# Revit family: Multiline Channel_ with grating - 24-05-2016 9
name_source: partatom
category: Generic Models
revit_build: Autodesk Revit 2014 (Build: 20130308_1515(x64)
units: mm (PartAtom-declared; Revit-internal decimal feet)

## types (12) — shared parameters
Anschrift = Postfach 320, 24755 Rendsburg
Assembly Code = D2040
Belastungsklasse = A 15 - E 600
Beschreibung = Entwässerungsrinne
Bottom depth = 20 mm  [stored 0.0656168 ft]
Breite = 135 mm  [stored 0.442913 ft]
Cut dist = 15.08 mm
Deponierfähigkeit Material Rinnenkörper = Abfallschlüssel 170107 gem. Verordnung über das Europäische Abfallverzeichnis
Einbauempfehlung, Qualität und Menge Ummantelungsbeton = http://www.aco-tiefbau.de
Einbauempfehlungen = http://www.aco-tiefbau.de
Farbe Kantenschutz = silber
Farbe Rinnenkörper = braun
Fax = +40 (0) 4331 354358
Front void end(Common) = -12 mm  [stored -0.0393701 ft]
Gasket = Yes
Gasket end = 9.13 mm  [stored 0.0299541 ft]
L projection end = -82.5 mm
L projection start = -67.5 mm  [stored -0.221457 ft]
Lieferant = ACO Tiefbau Vertrieb GmbH
Material Kantenschutz = Stahl
Material Rinnenkörper = ACO Polymerbeton
Norm = DIN EN 1433:2002, CE - Kennzeichnung
Oberflächenschutz Kantenschutz = verzinkt
Preis / Stck = http://www.aco-tiefbau.de
Produktbroschüre = http://www.aco-tiefbau.de
Produktinformationen = http://www.aco-tiefbau.de
Produktname = ACO DRAIN Multiline V 100 S
R projection start = 67.5 mm  [stored 0.221457 ft]
Recyclingfähigkeit Material Kantenschutz = voll recyclingfähig
Recyclingfähigkeit Material Rinnenkörper = voll recyclingfähig
Telefon = +49 (0) 4331 354 500
URL = www.aco-tiefbau.de
Version = 1
entwickelt von = www.aco-tiefbau.de
hydraulische Leistungsfähigkeit = e_mail anwendungstechnik

## per-type parameters (varying)
| type | Abmessungen | Artikelnummer | Betreibs- und Wartungshinweise | Channel article number | Channel price / stk | Channel weight ( Kg ) | Channnel dimensions( L x W x H) | Gewicht | Grating | Grating number | Höhe | Länge | Outlet end | Outlet start | Profile | Projection | R projection end | Rear extrusion end | Rear extrusion start | Side cut | Type Comments | Void depth |
| 132330- Channel_1000_ lg_150_ht | 1000mm x 135mm x 150mm (LxWxH | 132330 | http://www.aco-tiefbau.de | 132330 | 57.25 EUR | 16.8 | 1000 x 135 x 150 | 15,0 Kg | A15 : 12665-Lochrost Edelstahl_500mm lang_1.4 kg | 1 | 150 mm | 1000 mm | -702 mm  [stored -2.30315 ft] | -700 mm  [stored -2.29659 ft] | 79 mm | No | 82.5 mm | -1011 mm  [stored -3.31693 ft] | -1000 mm  [stored -3.28084 ft] | 56.5 mm  [stored 0.185367 ft] | "ACO DRAIN Multiline V100S 0.0, Rinnenkörper ohne Sohlengefälle, 
serienmäßig mit EPDM Dichtung, 1000mm lang" | 93.5 mm |
| 132340- Channel_1000_ lg_175_ht | 1000mm x 135mm x 175mm (LxWxH) | 132340 | http://www.aco-tiefbau.de | 132340 | 57.25 EUR | 18.9 | 1000 x 135 x 175 | 17,1 Kg |  | 1 | 175 mm | 1000 mm | -702 mm  [stored -2.30315 ft] | -700 mm  [stored -2.29659 ft] | 104 mm  [stored 0.341207 ft] | No | 82.5 mm | -1011 mm  [stored -3.31693 ft] | -1000 mm  [stored -3.28084 ft] | 81.5 mm  [stored 0.267388 ft] | "ACO DRAIN Multiline V100S 5.0, Rinnenkörper ohne Sohlengefälle, 
serienmäßig mit EPDM Dichtung, 1000mm lang" | 118.5 mm  [stored 0.38878 ft] |
| 132350- Channel_1000_ lg_200_ht | 1000mm x 135mm x 200mm (LxWxH) | 132350 | http://www.aco-tiefbau.de | 132350 | 57.25 EUR | 21.0 | 1000 x 135 x 200 | 19,6 Kg |  | 2 | 200 mm | 1000 mm | -702 mm  [stored -2.30315 ft] | -700 mm  [stored -2.29659 ft] | 129 mm  [stored 0.423228 ft] | No | 82.5 mm | -1011 mm  [stored -3.31693 ft] | -1000 mm  [stored -3.28084 ft] | 106.5 mm  [stored 0.349409 ft] | "ACO DRAIN Multiline V100S 10.0, Rinnenkörper ohne Sohlengefälle, 
serienmäßig mit EPDM Dichtung, 1000mm lang" | 143.5 mm  [stored 0.470801 ft] |
| 132370- Channel_1000_ lg_250_ht | 1000mm x 135mm x 250mm (LxWxH) | 132370 | http://www.aco-tiefbau.de | 132370 | 57.25 EUR | 24.9 | 1000 x 135 x 250 | 22,3 Kg |  | 1 | 250 mm | 1000 mm | -702 mm  [stored -2.30315 ft] | -700 mm  [stored -2.29659 ft] | 179 mm | No | 82.5 mm | -1011 mm  [stored -3.31693 ft] | -1000 mm  [stored -3.28084 ft] | 156.5 mm | "ACO DRAIN Multiline V100S 20.0, Rinnenkörper ohne Sohlengefälle, 
serienmäßig mit EPDM Dichtung, 1000mm lang" | 193.5 mm |
| 132332- Channel_500_ lg_150_ht | 500mm x 135mm x 150mm (LxWxH) | 132332 | http://www.aco-tiefbau.de | 132332 | 43.50 EUR | 9.5 | 500 x 135 x 150 | 8,5 Kg |  | 2 | 150 mm | 500 mm | -135 mm | -51 mm | 79 mm | No | 82.5 mm | -511 mm  [stored -1.67651 ft] | -500 mm  [stored -1.64042 ft] | 56.5 mm  [stored 0.185367 ft] | "ACO DRAIN Multiline V100S 0.1, Rinnenkörper ohne Sohlengefälle, 
serienmäßig mit EPDM Dichtung, 500mm lang, mit seitlichen Vorformungen für Eck-, T- und Kreuzverbindungen" | 93.5 mm |
| 132342- Channel_500_ lg_175_ht | 500mm x 135mm x 175mm (LxWxH) | 132342 | http://www.aco-tiefbau.de | 132342 | 43.50 EUR | 10.6 | 500 x 135 x 175 | 9,4 Kg |  | 2 | 175 mm | 500 mm | -160 mm  [stored -0.524934 ft] | -51 mm | 104 mm  [stored 0.341207 ft] | No | 82.5 mm | -511 mm  [stored -1.67651 ft] | -500 mm  [stored -1.64042 ft] | 81.5 mm  [stored 0.267388 ft] | "ACO DRAIN Multiline V100S 5.1, Rinnenkörper ohne Sohlengefälle, serienmäßig mit EPDM Dichtung, 500mm lang, 
mit seitlichen Vorformungen für Eck-, T- und Kreuzverbindungen" | 118.5 mm  [stored 0.38878 ft] |
| 132352- Channel_500_ lg_200_ht | 500mm x 135mm x 200mm (LxWxH) | 132352 | http://www.aco-tiefbau.de
http://www.aco-tiefbau.de | 132352 | 43.50 EUR | 11.7 | 500 x 135 x 200 | 10,4 Kg |  | 2 | 200 mm | 500 mm | -185 mm  [stored -0.606955 ft] | -51 mm | 129 mm  [stored 0.423228 ft] | No | 156.24 mm | -511 mm  [stored -1.67651 ft] | -500 mm  [stored -1.64042 ft] | 106.5 mm  [stored 0.349409 ft] | "ACO DRAIN Multiline V100S 10.1, Rinnenkörper ohne Sohlengefälle, serienmäßig mit EPDM Dichtung, 500mm lang, 
mit seitlichen Vorformungen für Eck-, T- und Kreuzverbindungen" | 143.5 mm  [stored 0.470801 ft] |
| 132372- Channel_500_ lg_250_ht | 500mm x 135mm x 250mm (LxWxH) | 132372 | http://www.aco-tiefbau.de | 132372 | 43.50 EUR | 14.0 | 500 x 135 x 250 | 12,3 Kg |  | 2 | 250 mm | 500 mm | -235 mm | -51 mm | 179 mm | No | 82.5 mm | -511 mm  [stored -1.67651 ft] | -500 mm  [stored -1.64042 ft] | 156.5 mm | "ACO DRAIN Multiline V100S 20.1, Rinnenkörper ohne Sohlengefälle, 500mm lang, serienmäßig mit EPDM Dichtung, 
mit seitlichen Vorformungen für Eck-, T- und Kreuzverbindungen" | 193.5 mm |
| 132333- Channel_500_ lg_160_ht_DN/OD_110 | 500mm x 135mm x 160mm (LxWxH) | 132333 | http://www.aco-tiefbau.de | 132333 | 51.75 EUR | 10.5 | 500 x 135 x 160 | 10,5 Kg |  | 2 | 160 mm | 500 mm | -160 mm  [stored -0.524934 ft] | -51 mm | 89 mm | Yes | 82.5 mm | -511 mm  [stored -1.67651 ft] | -500 mm  [stored -1.64042 ft] | 60.27 mm |  | 103.5 mm |
| 132343- Channel_500_ lg_185_ht_ DN/OD_110 | 500mm x 135mm x 185mm (LxWxH) | 132343 | http://www.aco-tiefbau.de | 132343 | 51.75 EUR | 11.8 | 500 x 135 x 185 | 11,8 Kg |  | 2 | 185 mm | 500 mm | -185 mm  [stored -0.606955 ft] | -51 mm | 114 mm | Yes | 113.21 mm | -511 mm  [stored -1.67651 ft] | -500 mm  [stored -1.64042 ft] | 86.16 mm  [stored 0.282677 ft] |  | 128.5 mm |
| 132353- Channel_500_ lg_210_ht_ DN/OD_110 | 500mm x 135mm x 210mm (LxWxH) | 132353 | http://www.aco-tiefbau.de | 132353 | 51.75 EUR | 13.2 | 500 x 135 x 210 | 13,2 Kg |  | 2 | 210 mm | 500 mm | -210 mm  [stored -0.688976 ft] | -51 mm | 139 mm | Yes | 82.5 mm | -511 mm  [stored -1.67651 ft] | -500 mm  [stored -1.64042 ft] | 111.83 mm  [stored 0.366896 ft] |  | 153.5 mm |
| 132373- Channel_500_ lg_260_ht_ DN/OD_110 | 500mm x 135mm x 260mm (LxWxH) | 132372 | http://www.aco-tiefbau.de | 132373 | 51.75 EUR | 15.3 | 500 x 135 x 260 | 15,3Kg |  | 2 | 260 mm | 500 mm | -260 mm  [stored -0.853018 ft] | -51 mm | 189 mm | Yes | 82.5 mm | -511 mm  [stored -1.67651 ft] | -500 mm  [stored -1.64042 ft] | 162.76 mm | "ACO DRAIN Multiline V100S 20.1, Rinnenkörper ohne Sohlengefälle, 500mm lang, serienmäßig mit EPDM Dichtung, 
mit seitlichen Vorformungen für Eck-, T- und Kreuzverbindungen" | 203.5 mm |

note: [stored X ft] marks values corroborated as IEEE doubles in the binary element streams (Revit-internal decimal feet)

## geometry (parser evidence)
native form markers: Sweep x15
no freeform markers — native parametric forms only
